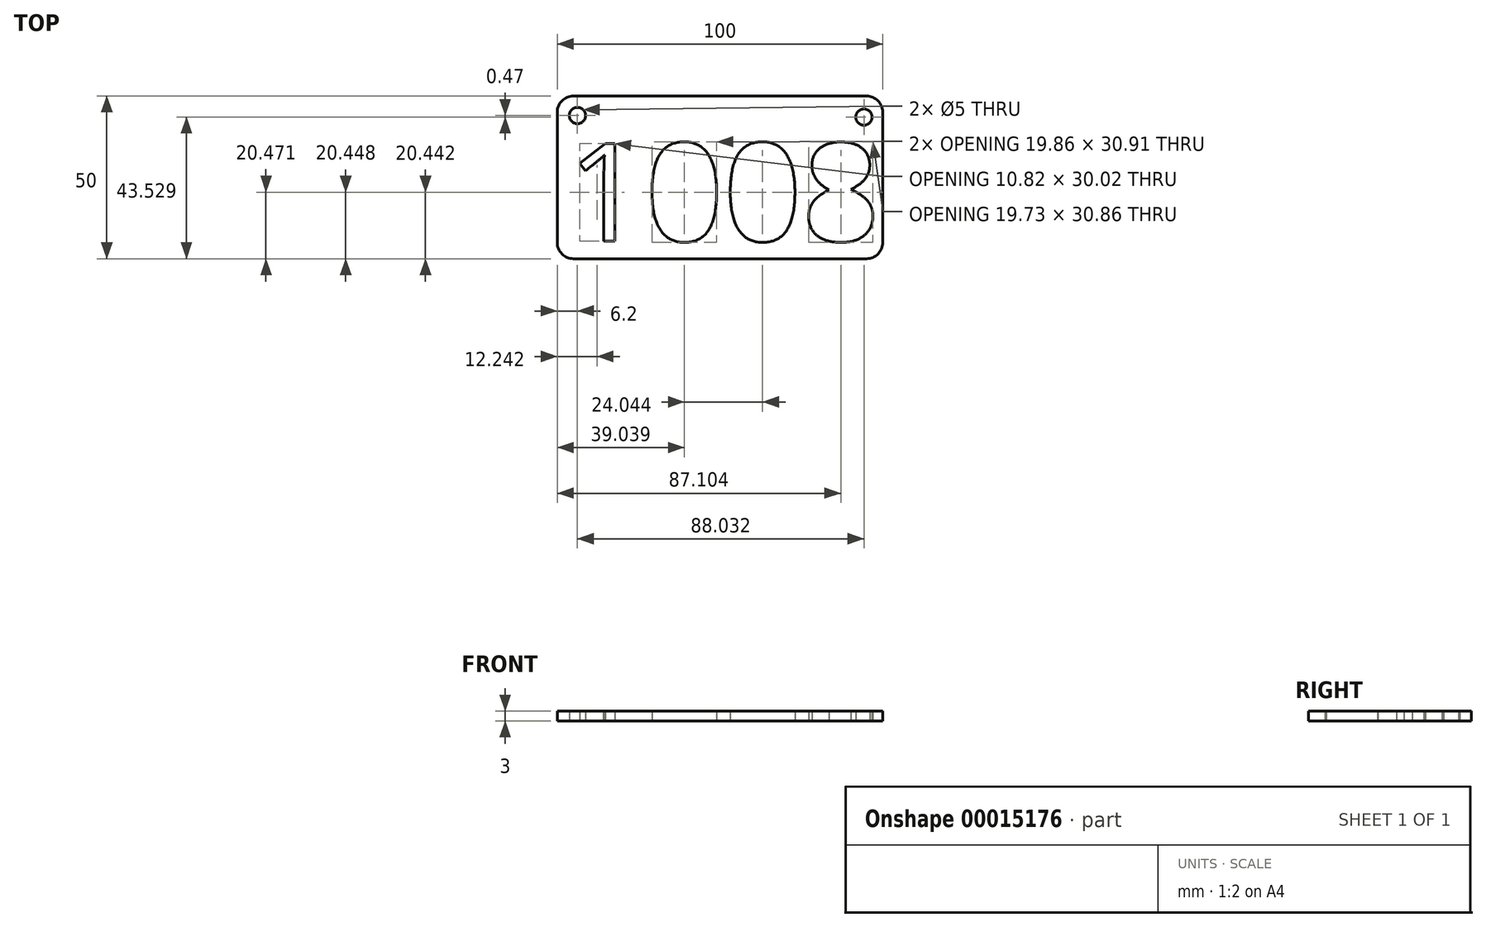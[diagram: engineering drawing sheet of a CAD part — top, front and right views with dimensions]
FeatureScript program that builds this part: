
annotation { "Feature Type Name" : "Feature", "Feature Type Description" : "" }
export const myFeature = defineFeature(function(context is Context, id is Id, definition is map)
    precondition{}
    {
        {
            var Q0;
            Q0=qCreatedBy(makeId("Top.planeOp"),FACE);
            var sketch = newSketch(context, id + "F0", { "sketchPlane" : qUnion([Q0])});
            skLineSegment(sketch, "E0.bottom", {"start": v(0, 0) * mm, "end": v(-100, 0) * mm});
            skLineSegment(sketch, "E0.top", {"start": v(0, 50) * mm, "end": v(-100, 50) * mm});
            skLineSegment(sketch, "E0.left", {"start": v(0, 0) * mm, "end": v(0, 50) * mm});
            skLineSegment(sketch, "E0.right", {"start": v(-100, 0) * mm, "end": v(-100, 50) * mm});
            skText(sketch, "E1", { "text": "1008", "fontName": "OpenSans-Regular.ttf"});
            skCircle(sketch, "E2", {"center": v(-93.8, 44) * mm, "radius": 2.5 * mm});
            skCircle(sketch, "E3", {"center": v(-5.77, 43.53) * mm, "radius": 2.5 * mm});
            const initialGuessF0  = {"E1": [-0.09703, 0.00543, 1, 0, 0.03028]};
            skSetInitialGuess(sketch, initialGuessF0);
            skSolve(sketch);
        }
        {
            var Q0;
            Q0=makeQuery(id+"F0.imprint","IMPRINT",FACE,{"disambiguationData":[TD([[makeQuery(id+"F0.imprint","IMPRINT",EDGE,{"derivedFrom":sQuery(id+"F0.wireOp",EDGE,"E0.bottom")}),-1.0]])]});
            extrude(context, id + "F1", {"entities" : qUnion([Q0]), "depth" : 3 * mm});
        }
        {
            var Q0;
            Q0=makeQuery(id+"F1.opExtrude","SWEPT_EDGE",EDGE,{"disambiguationData":[OSD([sQuery(id+"F0.wireOp",EDGE,"E0.top"),sQuery(id+"F0.wireOp",EDGE,"E0.left")])]});
            var Q1;
            Q1=makeQuery(id+"F1.opExtrude","SWEPT_EDGE",EDGE,{"disambiguationData":[OSD([sQuery(id+"F0.wireOp",EDGE,"E0.bottom"),sQuery(id+"F0.wireOp",EDGE,"E0.left")])]});
            var Q2;
            Q2=makeQuery(id+"F1.opExtrude","SWEPT_EDGE",EDGE,{"disambiguationData":[OSD([sQuery(id+"F0.wireOp",EDGE,"E0.top"),sQuery(id+"F0.wireOp",EDGE,"E0.right")])]});
            var Q3;
            Q3=makeQuery(id+"F1.opExtrude","SWEPT_EDGE",EDGE,{"disambiguationData":[OSD([sQuery(id+"F0.wireOp",EDGE,"E0.bottom"),sQuery(id+"F0.wireOp",EDGE,"E0.right")])]});
            fillet(context, id + "F2", {"entities" : qUnion([Q0, Q1, Q2, Q3]), "radius" : 5 * mm, "tangentPropagation" : true, "allowEdgeOverflow" : false});
        }
    });
